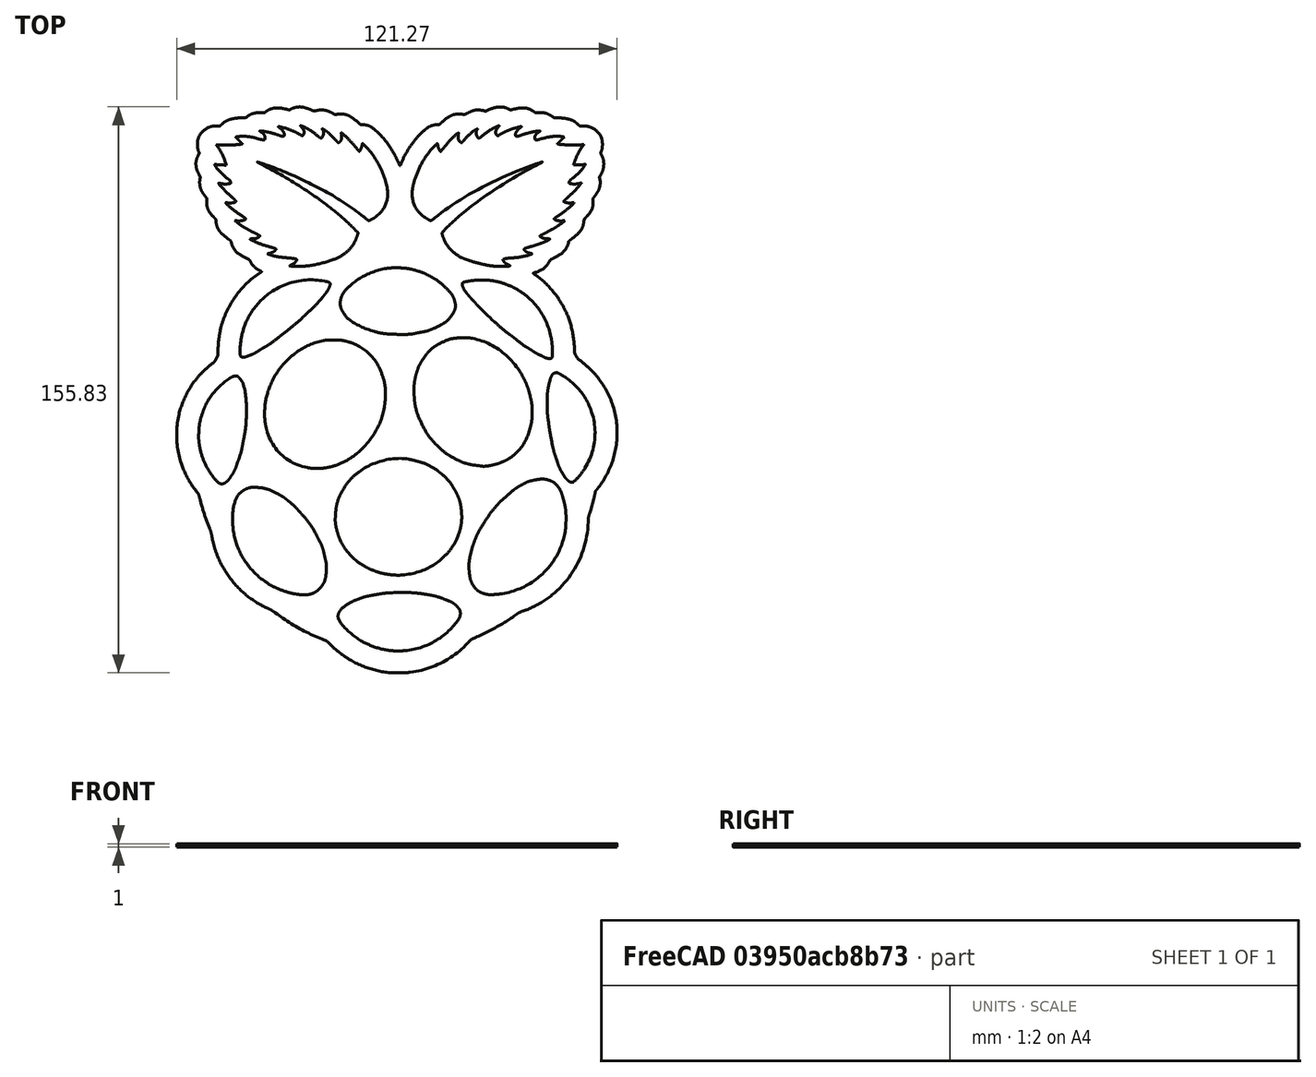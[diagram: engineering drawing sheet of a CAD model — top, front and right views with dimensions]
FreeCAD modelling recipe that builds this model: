
FCSTD DOCUMENT  (FreeCAD 0.19R)
Label: piLogo
License: All rights reserved
LicenseURL: http://en.wikipedia.org/wiki/All_rights_reserved
objects: Part::Feature×14, Part::Extrusion×14, Part::MultiFuse×1, Part::Cut×1
note: 30 computed .brp shape members not serialized (recipe doc carries the construction recipe); baked Part::Feature solids carry a one-line shape summary decoded from their .brp

FEATURE [Part::Feature] path94
  shape: bbox 121.7 x 156.1 x 2e-07 mm, 1 faces, 0 solids (baked)
FEATURE [Part::Feature] path94001
  shape: bbox 33.87 x 16.22 x 2e-07 mm, 1 faces, 0 solids (baked)
FEATURE [Part::Feature] path94002
  shape: bbox 26 x 29.63 x 2e-07 mm, 1 faces, 0 solids (baked)
FEATURE [Part::Feature] path94003
  shape: bbox 26.79 x 32.02 x 2e-07 mm, 1 faces, 0 solids (baked)
FEATURE [Part::Feature] path94004
  shape: bbox 34.84 x 32.78 x 2e-07 mm, 1 faces, 0 solids (baked)
FEATURE [Part::Feature] path94005
  shape: bbox 13.29 x 29.98 x 2e-07 mm, 1 faces, 0 solids (baked)
FEATURE [Part::Feature] path94006
  shape: bbox 13.93 x 30.32 x 2e-07 mm, 1 faces, 0 solids (baked)
FEATURE [Part::Feature] path94007
  shape: bbox 33.34 x 35.47 x 2e-07 mm, 1 faces, 0 solids (baked)
FEATURE [Part::Feature] path94008
  shape: bbox 32.64 x 35.5 x 2e-07 mm, 1 faces, 0 solids (baked)
FEATURE [Part::Feature] path94009
  shape: bbox 25.13 x 21.74 x 2e-07 mm, 1 faces, 0 solids (baked)
FEATURE [Part::Feature] path94010
  shape: bbox 24.8 x 21.99 x 2e-07 mm, 1 faces, 0 solids (baked)
FEATURE [Part::Feature] path94011
  shape: bbox 31.87 x 18.53 x 2e-07 mm, 1 faces, 0 solids (baked)
FEATURE [Part::Feature] path94012
  shape: bbox 47.88 x 38.81 x 2e-07 mm, 1 faces, 0 solids (baked)
FEATURE [Part::Feature] path94013
  shape: bbox 47.72 x 38.86 x 2e-07 mm, 1 faces, 0 solids (baked)
FEATURE [Part::Extrusion] Extrude
  Base = -> path94
  Dir = (0,0,1)
  DirMode = 0
  FaceMakerClass = Part::FaceMakerBullseye
  LengthFwd = 1
  LengthRev = 0
  Solid = false
  Symmetric = false
FEATURE [Part::Extrusion] Extrude001
  Base = -> path94001
  Dir = (0,0,1)
  DirMode = 0
  FaceMakerClass = Part::FaceMakerBullseye
  LengthFwd = 1
  LengthRev = 0
  Solid = false
  Symmetric = false
FEATURE [Part::Extrusion] Extrude002
  Base = -> path94002
  Dir = (0,0,1)
  DirMode = 0
  FaceMakerClass = Part::FaceMakerBullseye
  LengthFwd = 1
  LengthRev = 0
  Solid = false
  Symmetric = false
FEATURE [Part::Extrusion] Extrude003
  Base = -> path94003
  Dir = (0,0,1)
  DirMode = 0
  FaceMakerClass = Part::FaceMakerBullseye
  LengthFwd = 1
  LengthRev = 0
  Solid = false
  Symmetric = false
FEATURE [Part::Extrusion] Extrude004
  Base = -> path94004
  Dir = (0,0,1)
  DirMode = 0
  FaceMakerClass = Part::FaceMakerBullseye
  LengthFwd = 1
  LengthRev = 0
  Solid = false
  Symmetric = false
FEATURE [Part::Extrusion] Extrude005
  Base = -> path94005
  Dir = (0,0,1)
  DirMode = 0
  FaceMakerClass = Part::FaceMakerBullseye
  LengthFwd = 1
  LengthRev = 0
  Solid = false
  Symmetric = false
FEATURE [Part::Extrusion] Extrude006
  Base = -> path94006
  Dir = (0,0,1)
  DirMode = 0
  FaceMakerClass = Part::FaceMakerBullseye
  LengthFwd = 1
  LengthRev = 0
  Solid = false
  Symmetric = false
FEATURE [Part::Extrusion] Extrude007
  Base = -> path94007
  Dir = (0,0,1)
  DirMode = 0
  FaceMakerClass = Part::FaceMakerBullseye
  LengthFwd = 1
  LengthRev = 0
  Solid = false
  Symmetric = false
FEATURE [Part::Extrusion] Extrude008
  Base = -> path94008
  Dir = (0,0,1)
  DirMode = 0
  FaceMakerClass = Part::FaceMakerBullseye
  LengthFwd = 1
  LengthRev = 0
  Solid = false
  Symmetric = false
FEATURE [Part::Extrusion] Extrude009
  Base = -> path94009
  Dir = (0,0,1)
  DirMode = 0
  FaceMakerClass = Part::FaceMakerBullseye
  LengthFwd = 1
  LengthRev = 0
  Solid = false
  Symmetric = false
FEATURE [Part::Extrusion] Extrude010
  Base = -> path94010
  Dir = (0,0,1)
  DirMode = 0
  FaceMakerClass = Part::FaceMakerBullseye
  LengthFwd = 1
  LengthRev = 0
  Solid = false
  Symmetric = false
FEATURE [Part::Extrusion] Extrude011
  Base = -> path94011
  Dir = (0,0,1)
  DirMode = 0
  FaceMakerClass = Part::FaceMakerBullseye
  LengthFwd = 1
  LengthRev = 0
  Solid = false
  Symmetric = false
FEATURE [Part::Extrusion] Extrude012
  Base = -> path94012
  Dir = (0,0,1)
  DirMode = 0
  FaceMakerClass = Part::FaceMakerBullseye
  LengthFwd = 1
  LengthRev = 0
  Solid = false
  Symmetric = false
FEATURE [Part::Extrusion] Extrude013
  Base = -> path94013
  Dir = (0,0,1)
  DirMode = 0
  FaceMakerClass = Part::FaceMakerBullseye
  LengthFwd = 1
  LengthRev = 0
  Solid = false
  Symmetric = false
FEATURE [Part::MultiFuse] Fusion
  Shapes = -> [Extrude001,Extrude002,Extrude003,Extrude004,Extrude005,Extrude006,Extrude007,Extrude008,Extrude009,Extrude010,Extrude011,Extrude012,Extrude013]
FEATURE [Part::Cut] Cut
  Base = -> Extrude
  Tool = -> Fusion
